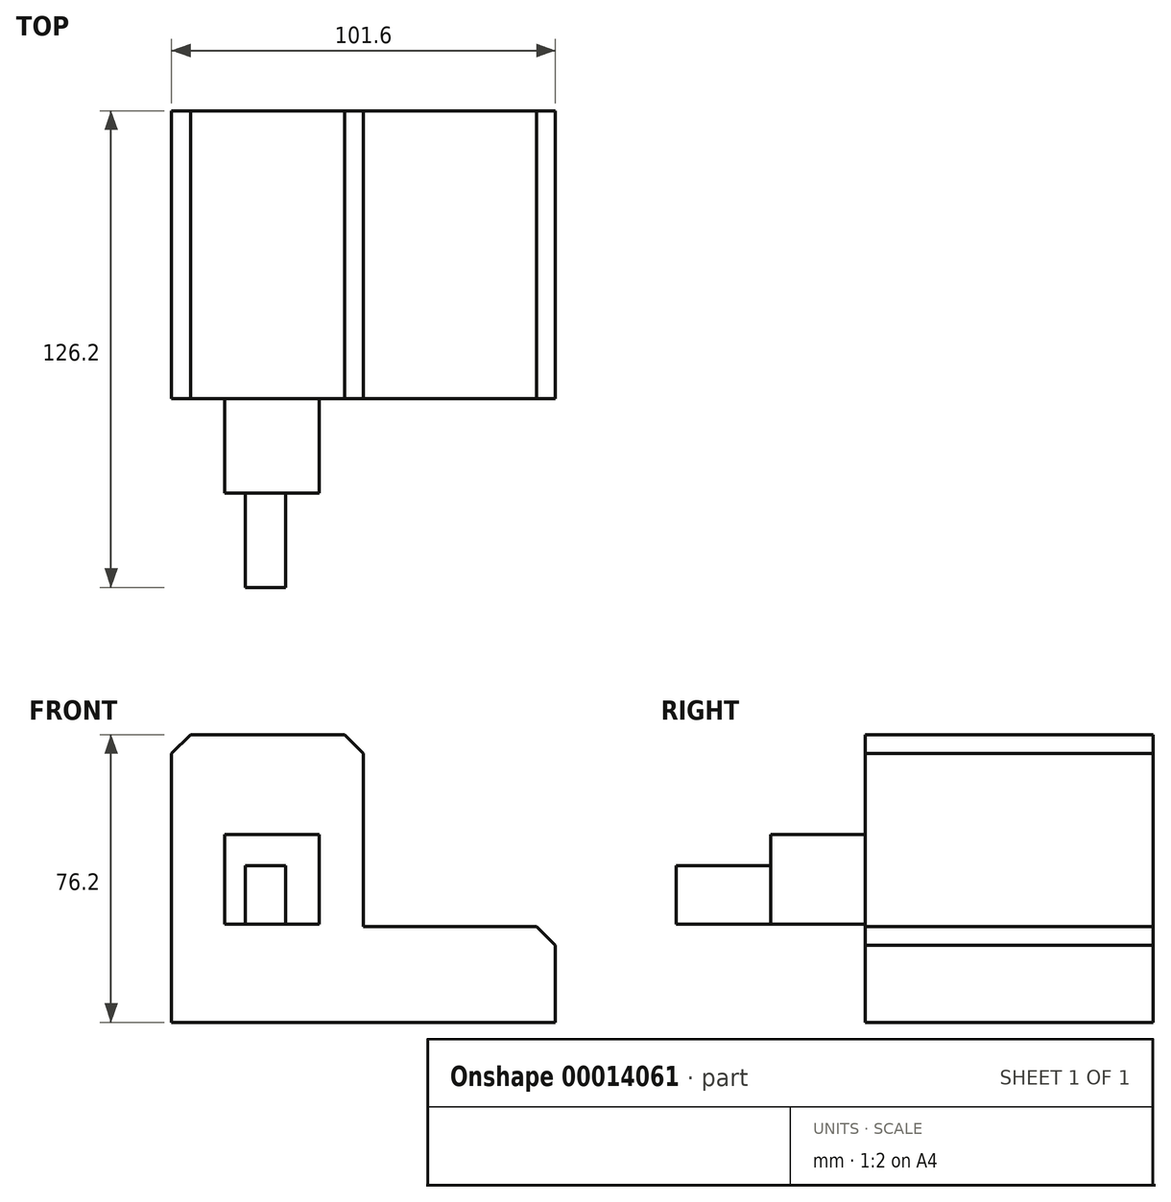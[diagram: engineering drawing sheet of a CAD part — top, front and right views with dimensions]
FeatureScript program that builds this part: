
annotation { "Feature Type Name" : "Feature", "Feature Type Description" : "" }
export const myFeature = defineFeature(function(context is Context, id is Id, definition is map)
    precondition{}
    {
        {
            var Q0;
            Q0=qCreatedBy(makeId("Top.planeOp"),FACE);
            var sketch = newSketch(context, id + "F0", { "sketchPlane" : qUnion([Q0])});
            skLineSegment(sketch, "E0.bottom", {"start": v(-47.42, 32.83) * mm, "end": v(54.18, 32.83) * mm});
            skLineSegment(sketch, "E0.top", {"start": v(-47.42, -43.37) * mm, "end": v(54.18, -43.37) * mm});
            skLineSegment(sketch, "E0.left", {"start": v(-47.42, 32.83) * mm, "end": v(-47.42, -43.37) * mm});
            skLineSegment(sketch, "E0.right", {"start": v(54.18, 32.83) * mm, "end": v(54.18, -43.37) * mm});
            skSolve(sketch);
        }
        {
            var Q0;
            Q0 = qSketchRegion(id + "F0", true);
            extrude(context, id + "F1", {"entities" : qUnion([Q0]), "depth" : 25.4 * mm});
        }
        {
            var Q0;
            Q0=makeQuery(id+"F1.opExtrude","CAP_FACE",FACE,{"disambiguationData":[OSD([sQuery(id+"F0.wireOp",EDGE,"E0.bottom"),sQuery(id+"F0.wireOp",EDGE,"E0.top"),sQuery(id+"F0.wireOp",EDGE,"E0.left"),sQuery(id+"F0.wireOp",EDGE,"E0.right")])],"isStart":false});
            var sketch = newSketch(context, id + "F2", { "sketchPlane" : qUnion([Q0])});
            skLineSegment(sketch, "E1.bottom", {"start": v(-47.42, 32.83) * mm, "end": v(3.38, 32.83) * mm});
            skLineSegment(sketch, "E1.top", {"start": v(-47.42, -43.37) * mm, "end": v(3.38, -43.37) * mm});
            skLineSegment(sketch, "E1.left", {"start": v(-47.42, 32.83) * mm, "end": v(-47.42, -43.37) * mm});
            skLineSegment(sketch, "E1.right", {"start": v(3.38, 32.83) * mm, "end": v(3.38, -43.37) * mm});
            skSolve(sketch);
        }
        {
            var Q0;
            Q0 = qSketchRegion(id + "F2", true);
            extrude(context, id + "F3", {"entities" : qUnion([Q0]), "operationType" : NewBodyOperationType.ADD, "depth" : 50.8 * mm});
        }
        {
            var Q0;
            Q0=makeQuery(id+"F3.boolean.opBoolean","MERGE",FACE,{"derivedFrom":[makeQuery(id+"F1.opExtrude","SWEPT_FACE",FACE,{"disambiguationData":[OSD([sQuery(id+"F0.wireOp",EDGE,"E0.top")])]}),makeQuery(id+"F3.opExtrude","SWEPT_FACE",FACE,{"disambiguationData":[OSD([sQuery(id+"F2.wireOp",EDGE,"E1.top")])]})]});
            var sketch = newSketch(context, id + "F4", { "sketchPlane" : qUnion([Q0])});
            skLineSegment(sketch, "E2.bottom", {"start": v(-33.42, 49.7) * mm, "end": v(-8.42, 49.7) * mm});
            skLineSegment(sketch, "E2.top", {"start": v(-33.42, 26) * mm, "end": v(-8.42, 26) * mm});
            skLineSegment(sketch, "E2.left", {"start": v(-33.42, 49.7) * mm, "end": v(-33.42, 26) * mm});
            skLineSegment(sketch, "E2.right", {"start": v(-8.42, 49.7) * mm, "end": v(-8.42, 26) * mm});
            skSolve(sketch);
        }
        {
            var Q0;
            Q0=makeQuery(id+"F4.imprint","IMPRINT",FACE,{"disambiguationData":[TD([[makeQuery(id+"F4.imprint","IMPRINT",EDGE,{"derivedFrom":sQuery(id+"F4.wireOp",EDGE,"E2.bottom")}),-1.0]])]});
            extrude(context, id + "F5", {"entities" : qUnion([Q0]), "operationType" : NewBodyOperationType.ADD, "depth" : 25 * mm});
        }
        {
            var Q0;
            Q0=makeQuery(id+"F5.opExtrude","CAP_FACE",FACE,{"disambiguationData":[OSD([sQuery(id+"F4.wireOp",EDGE,"E2.bottom"),sQuery(id+"F4.wireOp",EDGE,"E2.top"),sQuery(id+"F4.wireOp",EDGE,"E2.left"),sQuery(id+"F4.wireOp",EDGE,"E2.right")])],"isStart":false});
            var sketch = newSketch(context, id + "F6", { "sketchPlane" : qUnion([Q0])});
            skLineSegment(sketch, "E3.bottom", {"start": v(-27.95, 41.47) * mm, "end": v(-17.25, 41.47) * mm});
            skLineSegment(sketch, "E3.top", {"start": v(-27.95, 26) * mm, "end": v(-17.25, 26) * mm});
            skLineSegment(sketch, "E3.left", {"start": v(-27.95, 41.47) * mm, "end": v(-27.95, 26) * mm});
            skLineSegment(sketch, "E3.right", {"start": v(-17.25, 41.47) * mm, "end": v(-17.25, 26) * mm});
            skSolve(sketch);
        }
        {
            var Q0;
            Q0 = qSketchRegion(id + "F6", true);
            extrude(context, id + "F7", {"entities" : qUnion([Q0]), "operationType" : NewBodyOperationType.ADD, "depth" : 25 * mm});
        }
        {
            var Q0;
            Q0=makeQuery(id+"F3.opExtrude","CAP_EDGE",EDGE,{"disambiguationData":[OSD([sQuery(id+"F2.wireOp",EDGE,"E1.left")])],"isStart":false});
            var Q1;
            Q1=makeQuery(id+"F3.opExtrude","CAP_EDGE",EDGE,{"disambiguationData":[OSD([sQuery(id+"F2.wireOp",EDGE,"E1.right")])],"isStart":false});
            var Q2;
            Q2=makeQuery(id+"F3.opExtrude","CAP_EDGE",EDGE,{"disambiguationData":[OSD([sQuery(id+"F2.wireOp",EDGE,"E1.right")])],"isStart":true});
            var Q3;
            Q3=makeQuery(id+"F1.opExtrude","CAP_EDGE",EDGE,{"disambiguationData":[OSD([sQuery(id+"F0.wireOp",EDGE,"E0.right")])],"isStart":false});
            chamfer(context, id + "F8", {"entities" : qUnion([Q0, Q1, Q2, Q3]), "width" : 5 * mm, "tangentPropagation" : true});
        }
    });
